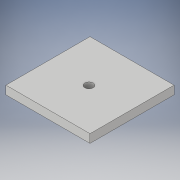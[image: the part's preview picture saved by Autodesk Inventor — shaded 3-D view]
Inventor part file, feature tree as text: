
AUTODESK INVENTOR PART (.ipt)
format: ipt  version: 2019.4 (Build 234330000, 330)  size: 94,208 bytes
history: native  units: in
note: dims shown in document units (in); Inventor stores cm internally (conversion verified against a paired STEP export)
features: sketch x2, extrude x1, hole x1
ambient origin geometry x8: Origin, YZ Plane, XZ Plane, XY Plane, X Axis, Y Axis, Z Axis, Center Point
bodies: Solid1 (feature_tree)
feature tree (4):
  extrude  "Extrusion1"  Depth=1.9685in
  hole  "Hole1"  [1 undecoded]
  sketch  "Sketch1"  dims[d0=1.9685in d1=1.9685in]
  sketch  "Sketch2"  dims[d2=0.1969in d3=0.0in d4=0.1969in d5=0.75in d6=0.375in d7=0.25in d8=0.5635in d9=1.0in d10=0.8108in]
note: 1 required parameter value undecoded (feature->parameter linkage not recoverable at this tier; creation-order binding heuristic only, values carry confidence <= 0.55)
